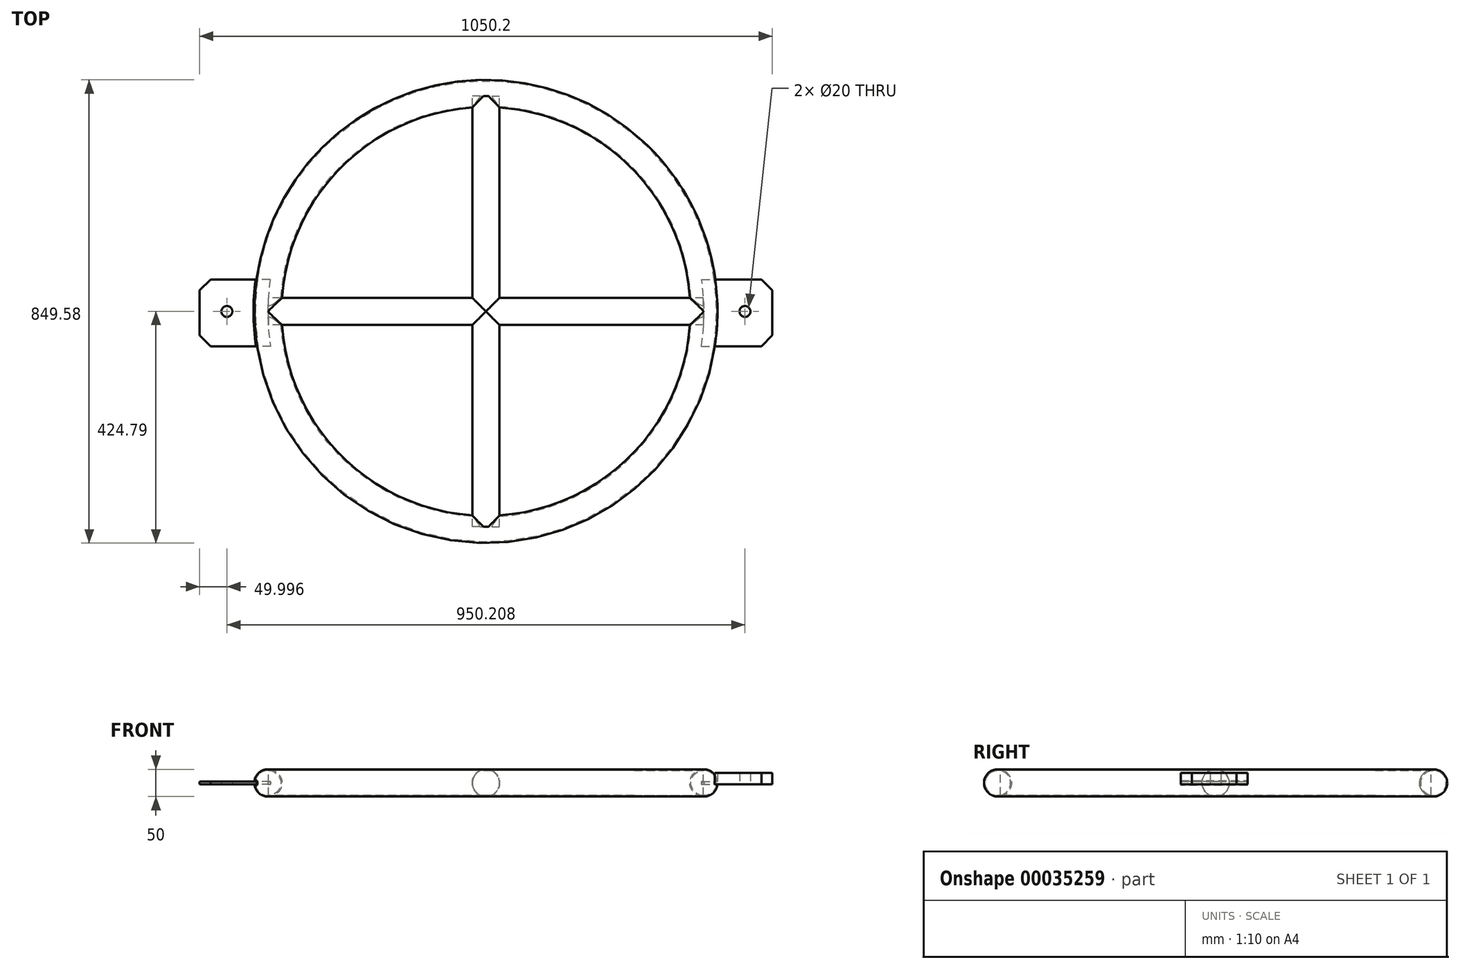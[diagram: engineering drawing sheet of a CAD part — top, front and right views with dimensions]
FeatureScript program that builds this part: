
annotation { "Feature Type Name" : "Feature", "Feature Type Description" : "" }
export const myFeature = defineFeature(function(context is Context, id is Id, definition is map)
    precondition{}
    {
        {
            var Q0;
            Q0=qCreatedBy(makeId("Top.planeOp"),FACE);
            var sketch = newSketch(context, id + "F0", { "sketchPlane" : qUnion([Q0])});
            skCircle(sketch, "E0", {"center": v(0, 0) * mm, "radius": 500 * mm});
            skSolve(sketch);
        }
        {
            var Q0;
            Q0=qCreatedBy(makeId("Front.planeOp"),FACE);
            var sketch = newSketch(context, id + "F1", { "sketchPlane" : qUnion([Q0])});
            skCircle(sketch, "E1", {"center": v(-399.79, 0) * mm, "radius": 25 * mm});
            skCircle(sketch, "E2", {"center": v(-399.79, 0) * mm, "radius": 23 * mm});
            skSolve(sketch);
        }
        {
            var Q0;
            Q0=makeQuery(id+"F1.imprint","IMPRINT",FACE,{"disambiguationData":[TD([[makeQuery(id+"F1.imprint","IMPRINT",EDGE,{"derivedFrom":sQuery(id+"F1.wireOp",EDGE,"E1")}),1.0]])]});
            var Q1;
            Q1=sQuery(id+"F0.wireOp",EDGE,"E0");
            sweep(context, id + "F2", {"profiles" : qUnion([Q0]), "path" : qUnion([Q1])});
        }
        {
            var Q0;
            Q0=qCreatedBy(makeId("Top.planeOp"),FACE);
            var sketch = newSketch(context, id + "F12", { "sketchPlane" : qUnion([Q0])});
            skLineSegment(sketch, "E3", {"start": v(0, -526.64) * mm, "end": v(0, 740.52) * mm});
            skLineSegment(sketch, "E4.MirrorCS", {"start": v(-394.88, -63.77) * mm, "end": v(-525.1, -63.77) * mm});
            skLineSegment(sketch, "E5.MirrorCS", {"start": v(-525.1, 58.51) * mm, "end": v(-525.1, -63.77) * mm});
            skLineSegment(sketch, "E6.MirrorCS", {"start": v(-395.7, 58.51) * mm, "end": v(-525.1, 58.51) * mm});
            skPoint(sketch, "E7.MirrorCS.end.orphan", {"position": v(-393.2, -63.77) * mm});
            skPoint(sketch, "E7.MirrorCS.start.orphan", {"position": v(-393.25, 58.51) * mm});
            skArc(sketch, "E8.0", {"start": v(-395.7, 58.51) * mm, "mid": v(-400, -2.66) * mm, "end": v(-394.88, -63.77) * mm});
            skPoint(sketch, "E9", {"position": v(-475.1, 0) * mm});
            skPoint(sketch, "E10.MirrorP", {"position": v(393.2, -63.77) * mm});
            skPoint(sketch, "E11.MirrorP", {"position": v(393.25, 58.51) * mm});
            skLineSegment(sketch, "E12.MirrorCS", {"start": v(395.7, 58.51) * mm, "end": v(525.1, 58.51) * mm});
            skLineSegment(sketch, "E13.MirrorCS", {"start": v(394.88, -63.77) * mm, "end": v(525.1, -63.77) * mm});
            skLineSegment(sketch, "E14.MirrorCS", {"start": v(525.1, 58.51) * mm, "end": v(525.1, -63.77) * mm});
            skPoint(sketch, "E15.MirrorP", {"position": v(475.1, 0) * mm});
            skArc(sketch, "E16.MirrorCS", {"start": v(395.7, 58.51) * mm, "mid": v(400, -2.66) * mm, "end": v(394.88, -63.77) * mm});
            skCircle(sketch, "E17", {"center": v(-475.1, 0) * mm, "radius": 10 * mm});
            skCircle(sketch, "E18", {"center": v(475.1, 0) * mm, "radius": 10 * mm});
            skSolve(sketch);
        }
        {
            var Q0;
            Q0 = qSketchRegion(id + "F12", true);
            extrude(context, id + "F3", {"entities" : qUnion([Q0]), "operationType" : NewBodyOperationType.ADD, "endBound" : BoundingType.SYMMETRIC, "depth" : 5 * mm});
        }
        {
            var Q0;
            Q0=makeQuery(id+"F3.boolean.opBoolean","INTERSECT",EDGE,{"derivedFrom":[makeQuery(id+"F2.opSweep","SWEPT_FACE",FACE,{"disambiguationData":[OSD([sQuery(id+"F0.wireOp",EDGE,"E0"),sQuery(id+"F1.wireOp",EDGE,"E1")])]}),makeQuery(id+"F3.opExtrude","CAP_FACE",FACE,{"disambiguationData":[OSD([sQuery(id+"F12.wireOp",EDGE,"b3787eb0-6675-4c12-b648-1101f684481c.bottom"),sQuery(id+"F12.wireOp",EDGE,"b3787eb0-6675-4c12-b648-1101f684481c.top"),sQuery(id+"F12.wireOp",EDGE,"b3787eb0-6675-4c12-b648-1101f684481c.right"),sQuery(id+"F12.wireOp",EDGE,"0e17f7c6-3074-4153-b44c-6c5b9fffc062.0")])],"isStart":false})]});
            var Q1;
            Q1=makeQuery(id+"F3.boolean.opBoolean","INTERSECT",EDGE,{"derivedFrom":[makeQuery(id+"F2.opSweep","SWEPT_FACE",FACE,{"disambiguationData":[OSD([sQuery(id+"F0.wireOp",EDGE,"E0"),sQuery(id+"F1.wireOp",EDGE,"E1")])]}),makeQuery(id+"F3.opExtrude","CAP_FACE",FACE,{"disambiguationData":[OSD([sQuery(id+"F12.wireOp",EDGE,"b3787eb0-6675-4c12-b648-1101f684481c.bottom"),sQuery(id+"F12.wireOp",EDGE,"b3787eb0-6675-4c12-b648-1101f684481c.top"),sQuery(id+"F12.wireOp",EDGE,"b3787eb0-6675-4c12-b648-1101f684481c.right"),sQuery(id+"F12.wireOp",EDGE,"0e17f7c6-3074-4153-b44c-6c5b9fffc062.0")])],"isStart":true})]});
            var Q2;
            Q2=makeQuery(id+"F3.boolean.opBoolean","INTERSECT",EDGE,{"derivedFrom":[makeQuery(id+"F2.opSweep","SWEPT_FACE",FACE,{"disambiguationData":[OSD([sQuery(id+"F0.wireOp",EDGE,"E0"),sQuery(id+"F1.wireOp",EDGE,"E1")])]}),makeQuery(id+"F3.opExtrude","CAP_FACE",FACE,{"disambiguationData":[OSD([sQuery(id+"F12.wireOp",EDGE,"E4.MirrorCS"),sQuery(id+"F12.wireOp",EDGE,"E5.MirrorCS"),sQuery(id+"F12.wireOp",EDGE,"E6.MirrorCS"),sQuery(id+"F12.wireOp",EDGE,"E8.0")])],"isStart":true})]});
            var Q3;
            Q3=makeQuery(id+"F3.boolean.opBoolean","INTERSECT",EDGE,{"derivedFrom":[makeQuery(id+"F2.opSweep","SWEPT_FACE",FACE,{"disambiguationData":[OSD([sQuery(id+"F0.wireOp",EDGE,"E0"),sQuery(id+"F1.wireOp",EDGE,"E1")])]}),makeQuery(id+"F3.opExtrude","CAP_FACE",FACE,{"disambiguationData":[OSD([sQuery(id+"F12.wireOp",EDGE,"E4.MirrorCS"),sQuery(id+"F12.wireOp",EDGE,"E5.MirrorCS"),sQuery(id+"F12.wireOp",EDGE,"E6.MirrorCS"),sQuery(id+"F12.wireOp",EDGE,"E8.0")])],"isStart":false})]});
            chamfer(context, id + "F4", {"entities" : qUnion([Q0, Q1, Q2, Q3]), "width" : 2 * mm, "tangentPropagation" : true});
        }
        {
            var Q0;
            Q0=makeQuery(id+"F3.opExtrude","SWEPT_EDGE",EDGE,{"disambiguationData":[OSD([sQuery(id+"F12.wireOp",EDGE,"E4.MirrorCS"),sQuery(id+"F12.wireOp",EDGE,"E5.MirrorCS")])]});
            var Q1;
            Q1=makeQuery(id+"F3.opExtrude","SWEPT_EDGE",EDGE,{"disambiguationData":[OSD([sQuery(id+"F12.wireOp",EDGE,"E5.MirrorCS"),sQuery(id+"F12.wireOp",EDGE,"E6.MirrorCS")])]});
            var Q2;
            Q2=makeQuery(id+"F3.opExtrude","SWEPT_EDGE",EDGE,{"disambiguationData":[OSD([sQuery(id+"F12.wireOp",EDGE,"E12.MirrorCS"),sQuery(id+"F12.wireOp",EDGE,"E14.MirrorCS")])]});
            var Q3;
            Q3=makeQuery(id+"F3.opExtrude","SWEPT_EDGE",EDGE,{"disambiguationData":[OSD([sQuery(id+"F12.wireOp",EDGE,"E13.MirrorCS"),sQuery(id+"F12.wireOp",EDGE,"E14.MirrorCS")])]});
            chamfer(context, id + "F5", {"entities" : qUnion([Q0, Q1, Q2, Q3]), "width" : 20 * mm, "tangentPropagation" : true});
        }
        {
            var Q0;
            Q0=qCreatedBy(makeId("Right.planeOp"),FACE);
            var sketch = newSketch(context, id + "F6", { "sketchPlane" : qUnion([Q0])});
            skCircle(sketch, "E19", {"center": v(0, 0) * mm, "radius": 25 * mm});
            skSolve(sketch);
        }
        {
            var Q0;
            Q0 = qSketchRegion(id + "F6", true);
            var Q1;
            Q1=makeQuery(id+"F2.opSweep","SWEPT_FACE",FACE,{"disambiguationData":[OSD([sQuery(id+"F0.wireOp",EDGE,"E0"),sQuery(id+"F1.wireOp",EDGE,"E1")])]});
            extrude(context, id + "F7", {"entities" : qUnion([Q0]), "operationType" : NewBodyOperationType.ADD, "endBound" : BoundingType.SYMMETRIC, "endBoundEntityFace" : qUnion([Q1]), "depth" : 798.07 * mm});
        }
        {
            var Q0;
            Q0=qCreatedBy(makeId("Right.planeOp"),FACE);
            var sketch = newSketch(context, id + "F8", { "sketchPlane" : qUnion([Q0])});
            skLineSegment(sketch, "E20", {"start": v(0, 66.24) * mm, "end": v(0, -70.36) * mm, "construction": true});
            skSolve(sketch);
        }
        {
            var Q0;
            Q0=qCreatedBy(makeId("Front.planeOp"),FACE);
            var sketch = newSketch(context, id + "F9", { "sketchPlane" : qUnion([Q0])});
            skCircle(sketch, "E21", {"center": v(0, 0) * mm, "radius": 25 * mm});
            skSolve(sketch);
        }
        {
            var Q0;
            Q0 = qSketchRegion(id + "F9", true);
            extrude(context, id + "F10", {"entities" : qUnion([Q0]), "operationType" : NewBodyOperationType.ADD, "endBound" : BoundingType.SYMMETRIC, "depth" : 790 * mm});
        }
        {
            var Q0;
            {var subQ0=sQuery(id+"F12.wireOp",EDGE,"E14.MirrorCS");var subQ1=sQuery(id+"F12.wireOp",EDGE,"E12.MirrorCS");var subQ2=sQuery(id+"F12.wireOp",EDGE,"E13.MirrorCS");var subQ3=sQuery(id+"F12.wireOp",EDGE,"E18");Q0=makeQuery(id+"F3.boolean.opBoolean","SPLIT",FACE,{"disambiguationData":[TD([makeQuery(id+"F3.opExtrude","SWEPT_FACE",FACE,{"disambiguationData":[OSD([subQ0])]})])],"derivedFrom":makeQuery(id+"F3.opExtrude","CAP_FACE",FACE,{"disambiguationData":[OSD([subQ1,subQ2,subQ0,sQuery(id+"F12.wireOp",EDGE,"E16.MirrorCS"),subQ3])],"isStart":false})});}
            extrude(context, id + "F13", {"entities" : qUnion([Q0]), "operationType" : NewBodyOperationType.ADD, "depth" : 15.82 * mm});
        }
    });
